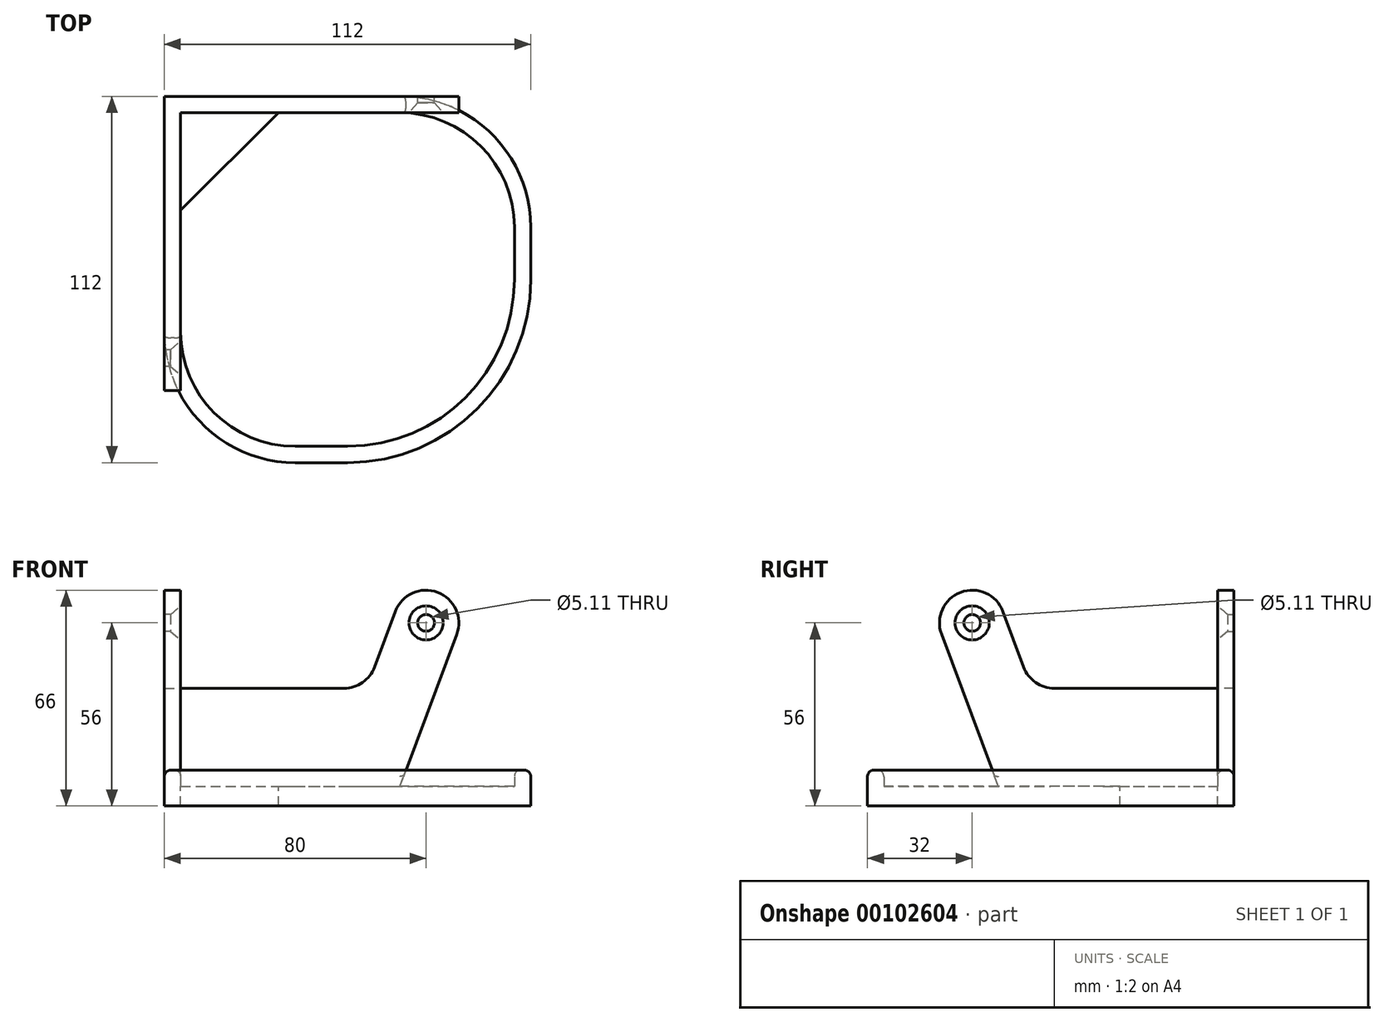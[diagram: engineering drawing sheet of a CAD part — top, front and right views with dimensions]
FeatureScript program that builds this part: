
annotation { "Feature Type Name" : "Feature", "Feature Type Description" : "" }
export const myFeature = defineFeature(function(context is Context, id is Id, definition is map)
    precondition{}
    {
        {
            var Q0;
            Q0=qCreatedBy(makeId("Top.planeOp"),FACE);
            var sketch = newSketch(context, id + "F0", { "sketchPlane" : qUnion([Q0])});
            skLineSegment(sketch, "E0.bottom", {"start": v(0, 0) * mm, "end": v(72, 0) * mm});
            skLineSegment(sketch, "E0.top", {"start": v(40, -112) * mm, "end": v(56, -112) * mm});
            skLineSegment(sketch, "E0.left", {"start": v(0, 0) * mm, "end": v(0, -72) * mm});
            skLineSegment(sketch, "E0.right", {"start": v(112, -40) * mm, "end": v(112, -56) * mm});
            skPoint(sketch, "E1.visualSharp", {"position": v(0, -112) * mm});
            skArc(sketch, "E1.filletArc", {"start": v(0, -72) * mm, "mid": v(11.72, -100.28) * mm, "end": v(40, -112) * mm});
            skPoint(sketch, "E2.visualSharp", {"position": v(112, 0) * mm});
            skArc(sketch, "E2.filletArc", {"start": v(112, -40) * mm, "mid": v(100.28, -11.72) * mm, "end": v(72, 0) * mm});
            skPoint(sketch, "E3.visualSharp", {"position": v(112, -112) * mm});
            skArc(sketch, "E3.filletArc", {"start": v(56, -112) * mm, "mid": v(95.6, -95.6) * mm, "end": v(112, -56) * mm});
            skLineSegment(sketch, "E4.0", {"start": v(5, -5) * mm, "end": v(5, -72) * mm});
            skLineSegment(sketch, "E4.1", {"start": v(5, -5) * mm, "end": v(72, -5) * mm});
            skLineSegment(sketch, "E4.2", {"start": v(40, -107) * mm, "end": v(56, -107) * mm});
            skArc(sketch, "E4.3", {"start": v(56, -107) * mm, "mid": v(92.06, -92.06) * mm, "end": v(107, -56) * mm});
            skLineSegment(sketch, "E4.4", {"start": v(107, -40) * mm, "end": v(107, -56) * mm});
            skArc(sketch, "E4.5", {"start": v(5, -72) * mm, "mid": v(15.25, -96.75) * mm, "end": v(40, -107) * mm});
            skArc(sketch, "E4.6", {"start": v(107, -40) * mm, "mid": v(96.75, -15.25) * mm, "end": v(72, -5) * mm});
            skLineSegment(sketch, "E5", {"start": v(5, -34.88) * mm, "end": v(34.88, -5) * mm});
            skLineSegment(sketch, "E6", {"start": v(5, -54.5) * mm, "end": v(57.5, -107) * mm, "construction": true});
            skLineSegment(sketch, "E7", {"start": v(57.5, -107) * mm, "end": v(107, -57.5) * mm, "construction": true});
            skLineSegment(sketch, "E8", {"start": v(107, -57.5) * mm, "end": v(54.5, -5) * mm, "construction": true});
            skLineSegment(sketch, "E9", {"start": v(54.5, -5) * mm, "end": v(5, -54.5) * mm, "construction": true});
            skLineSegment(sketch, "E10", {"start": v(5, -54.5) * mm, "end": v(107, -57.5) * mm, "construction": true});
            skLineSegment(sketch, "E11", {"start": v(29.75, -29.75) * mm, "end": v(19.94, -19.94) * mm, "construction": true});
            skCircle(sketch, "E12", {"center": v(56, -56) * mm, "radius": 51 * mm, "construction": true});
            skSolve(sketch);
        }
        {
            var Q0;
            Q0=qSketchRegion(id+"F0",true);
            var Q1;
            Q1=makeQuery(id+"F0.imprint","IMPRINT",FACE,{"disambiguationData":[TD([[makeQuery(id+"F0.imprint","IMPRINT",EDGE,{"derivedFrom":sQuery(id+"F0.wireOp",EDGE,"E4.2")}),1.0]])]});
            extrude(context, id + "F1", {"entities" : qUnion([Q0, Q1]), "oppositeDirection" : true, "depth" : 6 * mm});
        }
        {
            var Q0;
            Q0=qSketchRegion(id+"F0",true);
            extrude(context, id + "F2", {"entities" : qUnion([Q0]), "operationType" : NewBodyOperationType.ADD, "depth" : 5 * mm});
        }
        {
            var Q0;
            {var subQ0=sQuery(id+"F0.wireOp",EDGE,"E4.0");Q0=makeQuery(id+"F2.boolean.opBoolean","MERGE",FACE,{"derivedFrom":[makeQuery(id+"F1.opExtrude","SWEPT_FACE",FACE,{"disambiguationData":[OSD([subQ0])]}),makeQuery(id+"F2.opExtrude","SWEPT_FACE",FACE,{"disambiguationData":[OSD([subQ0])]})]});}
            var sketch = newSketch(context, id + "F3", { "sketchPlane" : qUnion([Q0])});
            skLineSegment(sketch, "E13", {"start": v(-72, 0) * mm, "end": v(-89.37, 46.5) * mm});
            skLineSegment(sketch, "E14", {"start": v(0, 30) * mm, "end": v(0, 0) * mm});
            skArc(sketch, "E15.filletArc", {"start": v(-80, 60) * mm, "mid": v(-88.22, 55.7) * mm, "end": v(-89.37, 46.5) * mm});
            skLineSegment(sketch, "E16", {"start": v(-72, 0) * mm, "end": v(0, 0) * mm});
            skArc(sketch, "E17", {"start": v(-70.63, 53.5) * mm, "mid": v(-74.3, 58.22) * mm, "end": v(-80, 60) * mm});
            skLineSegment(sketch, "E18", {"start": v(-70.63, 53.5) * mm, "end": v(-64.28, 36.5) * mm});
            skLineSegment(sketch, "E19", {"start": v(-54.92, 30) * mm, "end": v(0, 30) * mm});
            skPoint(sketch, "E20.visualSharp", {"position": v(-61.86, 30) * mm});
            skArc(sketch, "E20.filletArc", {"start": v(-64.28, 36.5) * mm, "mid": v(-60.62, 31.78) * mm, "end": v(-54.92, 30) * mm});
            skSolve(sketch);
        }
        {
            var Q0;
            Q0=qSketchRegion(id+"F3",true);
            var Q1;
            {var subQ0=sQuery(id+"F0.wireOp",EDGE,"E0.left");Q1=makeQuery(id+"F2.boolean.opBoolean","MERGE",FACE,{"derivedFrom":[makeQuery(id+"F1.opExtrude","SWEPT_FACE",FACE,{"disambiguationData":[OSD([subQ0])]}),makeQuery(id+"F2.opExtrude","SWEPT_FACE",FACE,{"disambiguationData":[OSD([subQ0])]})]});}
            extrude(context, id + "F4", {"entities" : qUnion([Q0]), "operationType" : NewBodyOperationType.ADD, "endBound" : BoundingType.UP_TO_SURFACE, "oppositeDirection" : true, "endBoundEntityFace" : qUnion([Q1]), "depth" : 25 * mm});
        }
        {
            var Q0;
            Q0=sQuery(id+"F3.wireOp",VERTEX,"E15.filletArc.center");
            var Q1;
            Q1=makeQuery(id+"F1.opExtrude","SWEPT_BODY",BODY,{"disambiguationData":[OSD([sQuery(id+"F0.wireOp",EDGE,"E0.bottom"),sQuery(id+"F0.wireOp",EDGE,"E0.top"),sQuery(id+"F0.wireOp",EDGE,"E0.left"),sQuery(id+"F0.wireOp",EDGE,"E0.right"),sQuery(id+"F0.wireOp",EDGE,"E1.filletArc"),sQuery(id+"F0.wireOp",EDGE,"E2.filletArc"),sQuery(id+"F0.wireOp",EDGE,"E3.filletArc"),sQuery(id+"F0.wireOp",EDGE,"E4.0"),sQuery(id+"F0.wireOp",EDGE,"E4.1"),sQuery(id+"F0.wireOp",EDGE,"E5")])]});
            hole(context, id + "F5", {"style" : HoleStyle.C_SINK, "endStyle" : HoleEndStyle.THROUGH, "standardTappedOrClearance" : lookupTablePath({ "standard" : "ANSI", "fit" : "Normal (ASME)", "size" : "#10", "type" : "Clearance" }), "standardBlindInLast" : lookupTablePath({ "fit" : "Free", "standard" : "ANSI", "size" : "#10", "type" : "Clearance" }), "holeDiameter" : 5.1 * mm, "cSinkDiameter" : 10.44 * mm, "cSinkAngle" : 82 * degree, "tappedDepth" : 12 * mm, "tapClearance" : 3, "locations" : qUnion([Q0]), "scope" : qUnion([Q1]), "startStyle" : HoleStartStyle.PART});
        }
        {
            var Q0;
            Q0=qCreatedBy(makeId("Front.planeOp"),FACE);
            var Q1;
            Q1=qCreatedBy(makeId("Right.planeOp"),FACE);
            cPlane(context, id + "F6", {"entities" : qUnion([Q0, Q1]), "cplaneType" : CPlaneType.MID_PLANE, "offset" : 25 * mm, "width" : 150 * mm, "height" : 150 * mm});
        }
        {
            var Q0;
            Q0=makeQuery(id+"F1.opExtrude","SWEPT_BODY",BODY,{"disambiguationData":[OSD([sQuery(id+"F0.wireOp",EDGE,"E0.bottom"),sQuery(id+"F0.wireOp",EDGE,"E0.top"),sQuery(id+"F0.wireOp",EDGE,"E0.left"),sQuery(id+"F0.wireOp",EDGE,"E0.right"),sQuery(id+"F0.wireOp",EDGE,"E1.filletArc"),sQuery(id+"F0.wireOp",EDGE,"E2.filletArc"),sQuery(id+"F0.wireOp",EDGE,"E3.filletArc"),sQuery(id+"F0.wireOp",EDGE,"E4.0"),sQuery(id+"F0.wireOp",EDGE,"E4.1"),sQuery(id+"F0.wireOp",EDGE,"E5")])]});
            var Q1;
            Q1=qCreatedBy(id+"F6.planeOp",FACE);
            mirror(context, id + "F7", {"operationType" : NewBodyOperationType.ADD, "entities" : qUnion([Q0]), "mirrorPlane" : qUnion([Q1])});
        }
        {
            var Q0;
            Q0=makeQuery(id+"F2.opExtrude","CAP_EDGE",EDGE,{"disambiguationData":[OSD([sQuery(id+"F0.wireOp",EDGE,"E4.5")])],"isStart":true});
            var Q1;
            Q1=makeQuery(id+"F2.opExtrude","CAP_EDGE",EDGE,{"disambiguationData":[OSD([sQuery(id+"F0.wireOp",EDGE,"E4.4")])],"isStart":false});
            var Q2;
            Q2=makeQuery(id+"F2.opExtrude","CAP_EDGE",EDGE,{"disambiguationData":[OSD([sQuery(id+"F0.wireOp",EDGE,"E3.filletArc")])],"isStart":false});
            var Q3;
            {var subQ0=sQuery(id+"F0.wireOp",EDGE,"E4.1");var subQ1=sQuery(id+"F0.wireOp",EDGE,"E4.0");Q3=makeQuery(id+"F2.boolean.opBoolean","MERGE",EDGE,{"derivedFrom":[makeQuery(id+"F1.opExtrude","SWEPT_EDGE",EDGE,{"disambiguationData":[OSD([subQ1,subQ0])]}),makeQuery(id+"F2.opExtrude","SWEPT_EDGE",EDGE,{"disambiguationData":[OSD([subQ1,subQ0])]})]});}
            fillet(context, id + "F8", {"entities" : qUnion([Q0, Q1, Q2, Q3]), "radius" : 2 * mm, "tangentPropagation" : true, "allowEdgeOverflow" : false});
        }
    });
